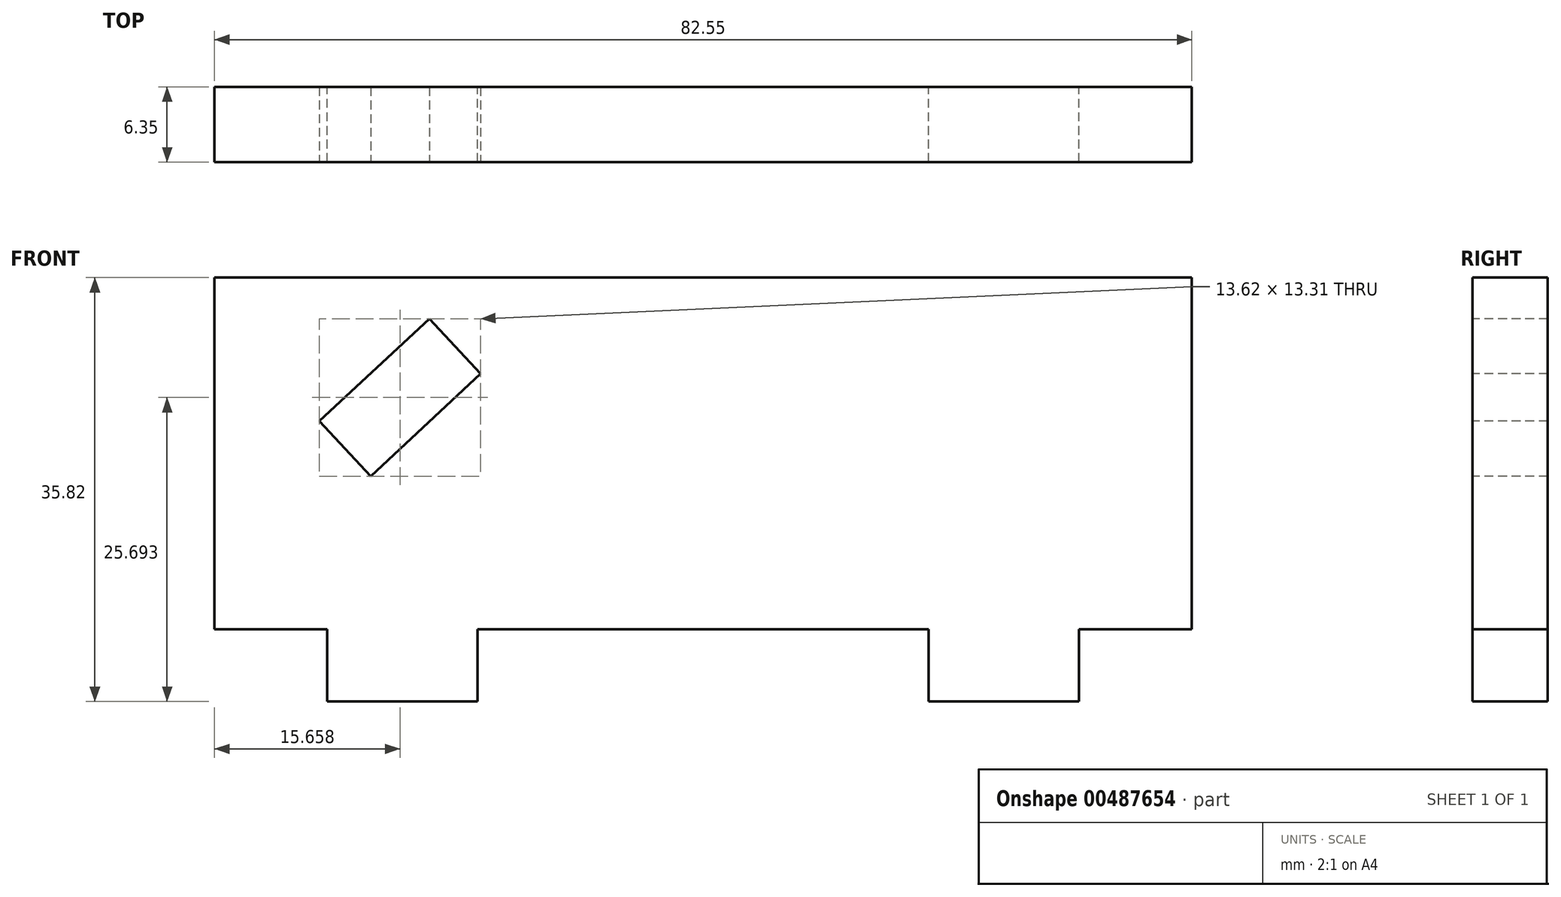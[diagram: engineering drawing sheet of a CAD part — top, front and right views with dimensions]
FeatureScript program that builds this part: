
annotation { "Feature Type Name" : "Feature", "Feature Type Description" : "" }
export const myFeature = defineFeature(function(context is Context, id is Id, definition is map)
    precondition{}
    {
        {
            var Q0;
            Q0=qCreatedBy(makeId("Front.planeOp"),FACE);
            var sketch = newSketch(context, id + "F0", { "sketchPlane" : qUnion([Q0])});
            skLineSegment(sketch, "E0.bottom", {"start": v(0, 0) * mm, "end": v(82.55, 0) * mm});
            skLineSegment(sketch, "E0.top", {"start": v(0, 29.72) * mm, "end": v(82.55, 29.72) * mm});
            skLineSegment(sketch, "E0.left", {"start": v(0, 0) * mm, "end": v(0, 29.72) * mm});
            skLineSegment(sketch, "E0.right", {"start": v(82.55, 0) * mm, "end": v(82.55, 29.72) * mm});
            skLineSegment(sketch, "E1.bottom", {"start": v(9.53, 0) * mm, "end": v(22.23, 0) * mm});
            skLineSegment(sketch, "E1.top", {"start": v(9.53, -6.1) * mm, "end": v(22.23, -6.1) * mm});
            skLineSegment(sketch, "E1.left", {"start": v(9.53, 0) * mm, "end": v(9.53, -6.1) * mm});
            skLineSegment(sketch, "E1.right", {"start": v(22.23, 0) * mm, "end": v(22.23, -6.1) * mm});
            skLineSegment(sketch, "E2.bottom", {"start": v(60.33, 0) * mm, "end": v(73.03, 0) * mm});
            skLineSegment(sketch, "E2.top", {"start": v(60.33, -6.1) * mm, "end": v(73.03, -6.1) * mm});
            skLineSegment(sketch, "E2.left", {"start": v(60.33, 0) * mm, "end": v(60.33, -6.1) * mm});
            skLineSegment(sketch, "E2.right", {"start": v(73.03, 0) * mm, "end": v(73.03, -6.1) * mm});
            skSolve(sketch);
        }
        {
            var Q0;
            {Q0=qUnion([makeQuery(id+"F0.imprint","IMPRINT",FACE,{"disambiguationData":[TD([[makeQuery(id+"F0.imprint","IMPRINT",EDGE,{"derivedFrom":sQuery(id+"F0.wireOp",EDGE,"E2.top")}),1.0]])]}),makeQuery(id+"F0.imprint","IMPRINT",FACE,{"disambiguationData":[TD([[makeQuery(id+"F0.imprint","IMPRINT",EDGE,{"derivedFrom":sQuery(id+"F0.wireOp",EDGE,"E1.top")}),1.0]])]}),makeQuery(id+"F0.imprint","IMPRINT",FACE,{"disambiguationData":[TD([[makeQuery(id+"F0.imprint","IMPRINT",EDGE,{"derivedFrom":sQuery(id+"F0.wireOp",EDGE,"E0.top")}),-1.0]])]})]);}
            extrude(context, id + "F1", {"entities" : qUnion([Q0]), "depth" : 6.35 * mm});
        }
        {
            var Q0;
            Q0=makeQuery(id+"F1.opExtrude","CAP_FACE",FACE,{"disambiguationData":[OSD([sQuery(id+"F0.wireOp",EDGE,"E0.bottom"),sQuery(id+"F0.wireOp",EDGE,"E0.top"),sQuery(id+"F0.wireOp",EDGE,"E0.left"),sQuery(id+"F0.wireOp",EDGE,"E0.right"),sQuery(id+"F0.wireOp",EDGE,"E1.top"),sQuery(id+"F0.wireOp",EDGE,"E1.left"),sQuery(id+"F0.wireOp",EDGE,"E1.right"),sQuery(id+"F0.wireOp",EDGE,"E2.top"),sQuery(id+"F0.wireOp",EDGE,"E2.left"),sQuery(id+"F0.wireOp",EDGE,"E2.right")])],"isStart":false});
            var sketch = newSketch(context, id + "F2", { "sketchPlane" : qUnion([Q0])});
            skLineSegment(sketch, "E3", {"start": v(15.67, 29.72) * mm, "end": v(15.67, 8.81) * mm, "construction": true});
            skLineSegment(sketch, "E4", {"start": v(18.85, 19.57) * mm, "end": v(11.08, 19.57) * mm, "construction": true});
            skPoint(sketch, "E4.endSnap0", {"position": v(12.5, 19.57) * mm});
            skPoint(sketch, "E5.middle", {"position": v(15.67, 19.6) * mm});
            skLineSegment(sketch, "E6", {"start": v(15.67, 19.6) * mm, "end": v(24.1, 27.47) * mm, "construction": true});
            skLineSegment(sketch, "E7", {"start": v(18.14, 26.25) * mm, "end": v(8.85, 17.58) * mm});
            skLineSegment(sketch, "E8.MirrorCS", {"start": v(22.47, 21.6) * mm, "end": v(13.18, 12.94) * mm});
            skLineSegment(sketch, "E9", {"start": v(18.14, 26.25) * mm, "end": v(13.18, 12.94) * mm, "construction": true});
            skLineSegment(sketch, "E10", {"start": v(22.47, 21.6) * mm, "end": v(8.85, 17.58) * mm, "construction": true});
            skLineSegment(sketch, "E11", {"start": v(18.14, 26.25) * mm, "end": v(22.47, 21.6) * mm});
            skLineSegment(sketch, "E12", {"start": v(8.85, 17.58) * mm, "end": v(13.18, 12.94) * mm});
            skSolve(sketch);
        }
        {
            var Q0;
            Q0 = qSketchRegion(id + "F2", true);
            extrude(context, id + "F3", {"entities" : qUnion([Q0]), "operationType" : NewBodyOperationType.REMOVE, "oppositeDirection" : true, "depth" : 25.4 * mm});
        }
    });
